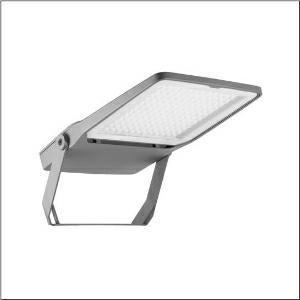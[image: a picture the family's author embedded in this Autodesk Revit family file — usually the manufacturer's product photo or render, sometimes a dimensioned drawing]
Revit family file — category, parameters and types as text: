
# Revit family: floodlight_fl_20_midi___pl43_5xa7682e3a1ac_f2b2
name_source: partatom
category: Lighting Fixtures
units: mm (PartAtom-declared; Revit-internal decimal feet)

## family parameters
Cut with Voids When Loaded = No
Host = Face
Light Source = No
Part Type = Normal
Room Calculation Point = No
Round Connector Dimension = Use Diameter
Shared = No

## types (1)
- --- (1 x LED 5000K / CRI = 70 (unbekannt), 28900 lm, 5000K)
    Apparent Load = 208 VA
    CIE Flux Codes = 32 74 99 100 100
    Color Rendering = 70
    Color Temperature = 5000K
    Default Elevation = 1800 mm
    Description = Floodlight FL 20 midi, floodlight, primary light control with lens, of plastic, primary optical cover: protective disc, of toughened safety glass, transparent, light distribution: PL43, light emission: direct distribution, primary light characteristic: asymmetric, installation type: surface-mounted, LED High Power LED, rated luminous flux: 28.900 lm, light colour: 750, colour temperature: 5000K, control gear: ECG Plus, control: flexible luminous flux parameterisation, time-dependent luminous flux control, digital communication interface, power reduction, overheat protection, electronic power reduction, with terminal, 5-pole, max. 2.5mm², mains connection: 220..240V, AC, 50/60Hz, rated input power: 208W, LED unit, of diecast aluminium, powder-coated, Siteco® metallic grey (DB 702S), length: 654 mm, width: 450 mm, height: 76mm, housing frame, of diecast aluminium, powder-coated, Siteco® metallic grey (DB 702S), mounting bracket, of steel, powder-coated, Siteco® metallic grey (DB 702S), DALIprotection rating (complete): IP66, insulation class (complete): insulation class II (safety insulation), certification: CE, ENEC, VDE, protection symbol: D, permissible ambient temperature for indoor applications: -40..+40°C, permissible ambient temperature for outdoor applications: -40..+50°C, standard: DIN EN 12944, packaging unit: 1 piece

Light Distribution: PL43
    Height = 76 mm
    Lamp = 1 x LED 5000K / CRI >= 70 (unbekannt)
    Lamp Light Flux = 28900 lm
    Lamp count = 1
    Length = 672 mm
    Luminous efficacy = 139 lm/W
    Manufacturer = Siteco
    ModVariant = No
    Model = 5XA7682E3A1AC
    Number of Poles = 1
    OnlyDefault = Yes
    Power Factor = 1
    Product Name = Floodlight FL 20 midi | PL43
    Product group = floodlight | pylon top
    ProductGroupID = 6101
    Protection Class = Protection class II
    Protection Degree = IP 66
    RLX_Detail_Level = 1
    RlxData = <blob elided: 97469 chars, md5=e1777d12>
    Socket = socket
    Standby Power = 0 W
    System Light Flux = 28900 lm
    System Power = 208 W
    Type Comments = factory setting: luminous flux: 100 % | dim-lin: 254 | 484 mA
    Type Image = l_1005943.jpg
    URL = http://relux.com
    VarID = @adj_143585
    Voltage = 0 V
    Weight = 0.00 kg
    Width = 450 mm

## geometry (parser evidence)
native form markers: Blend x4, Sweep x11
no freeform markers — native parametric forms only
